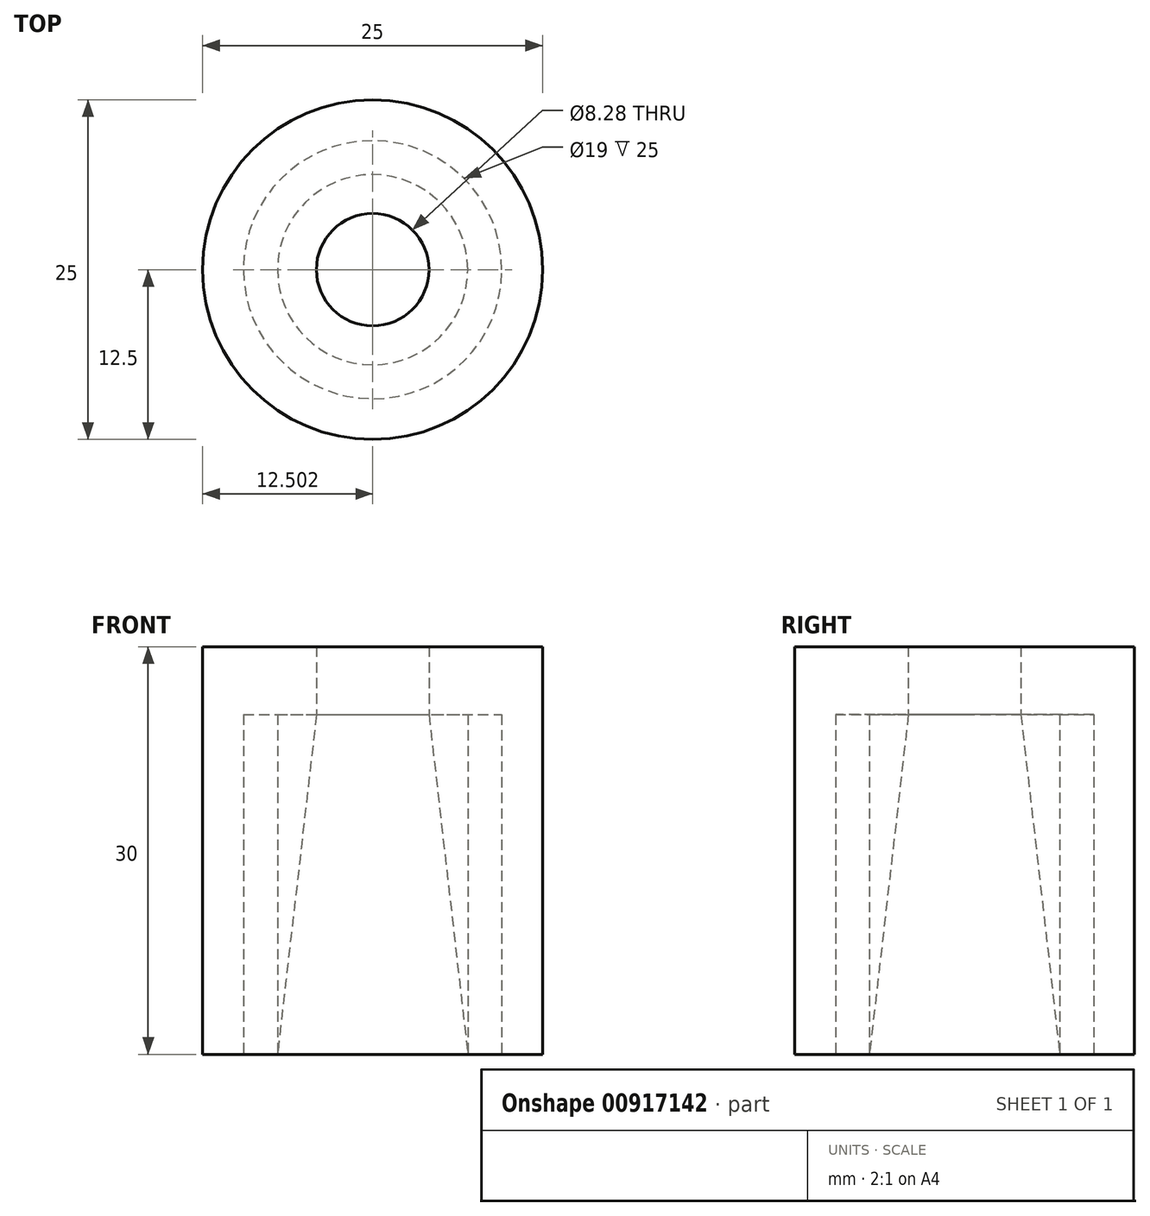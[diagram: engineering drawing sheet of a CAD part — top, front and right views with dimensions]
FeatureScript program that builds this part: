
annotation { "Feature Type Name" : "Feature", "Feature Type Description" : "" }
export const myFeature = defineFeature(function(context is Context, id is Id, definition is map)
    precondition{}
    {
        {
            var Q0;
            Q0=qCreatedBy(makeId("Front.planeOp"),FACE);
            var sketch = newSketch(context, id + "F0", { "sketchPlane" : qUnion([Q0])});
            skLineSegment(sketch, "E0", {"start": v(1.22, 30) * mm, "end": v(6.05, 30) * mm});
            skLineSegment(sketch, "E1", {"start": v(6.05, 30) * mm, "end": v(6.05, 0) * mm});
            skLineSegment(sketch, "E2", {"start": v(6.05, 0) * mm, "end": v(3.05, 0) * mm});
            skLineSegment(sketch, "E3", {"start": v(3.05, 0) * mm, "end": v(3.05, 25) * mm});
            skLineSegment(sketch, "E4", {"start": v(3.05, 25) * mm, "end": v(0.55, 25) * mm});
            skPoint(sketch, "E5.start.orphan", {"position": v(0.55, 0) * mm});
            skLineSegment(sketch, "E6", {"start": v(0.55, 25) * mm, "end": v(0.55, 0) * mm});
            skLineSegment(sketch, "E7", {"start": v(0.55, 0) * mm, "end": v(-2.31, 25) * mm});
            skLineSegment(sketch, "E8", {"start": v(-2.31, 30) * mm, "end": v(-2.31, 25) * mm});
            skLineSegment(sketch, "E9", {"start": v(-2.31, 30) * mm, "end": v(1.22, 30) * mm});
            skLineSegment(sketch, "E10", {"start": v(-6.45, 0) * mm, "end": v(-6.45, 35.52) * mm});
            skSolve(sketch);
        }
        {
            var Q0;
            Q0 = qSketchRegion(id + "F0", true);
            var Q1;
            Q1=sQuery(id+"F0.wireOp",EDGE,"E10");
            revolve(context, id + "F1", {"surfaceOperationType" : NewSurfaceOperationType.NEW, "entities" : qUnion([Q0]), "axis" : qUnion([Q1]), "revolveType" : RevolveType.FULL});
        }
    });
